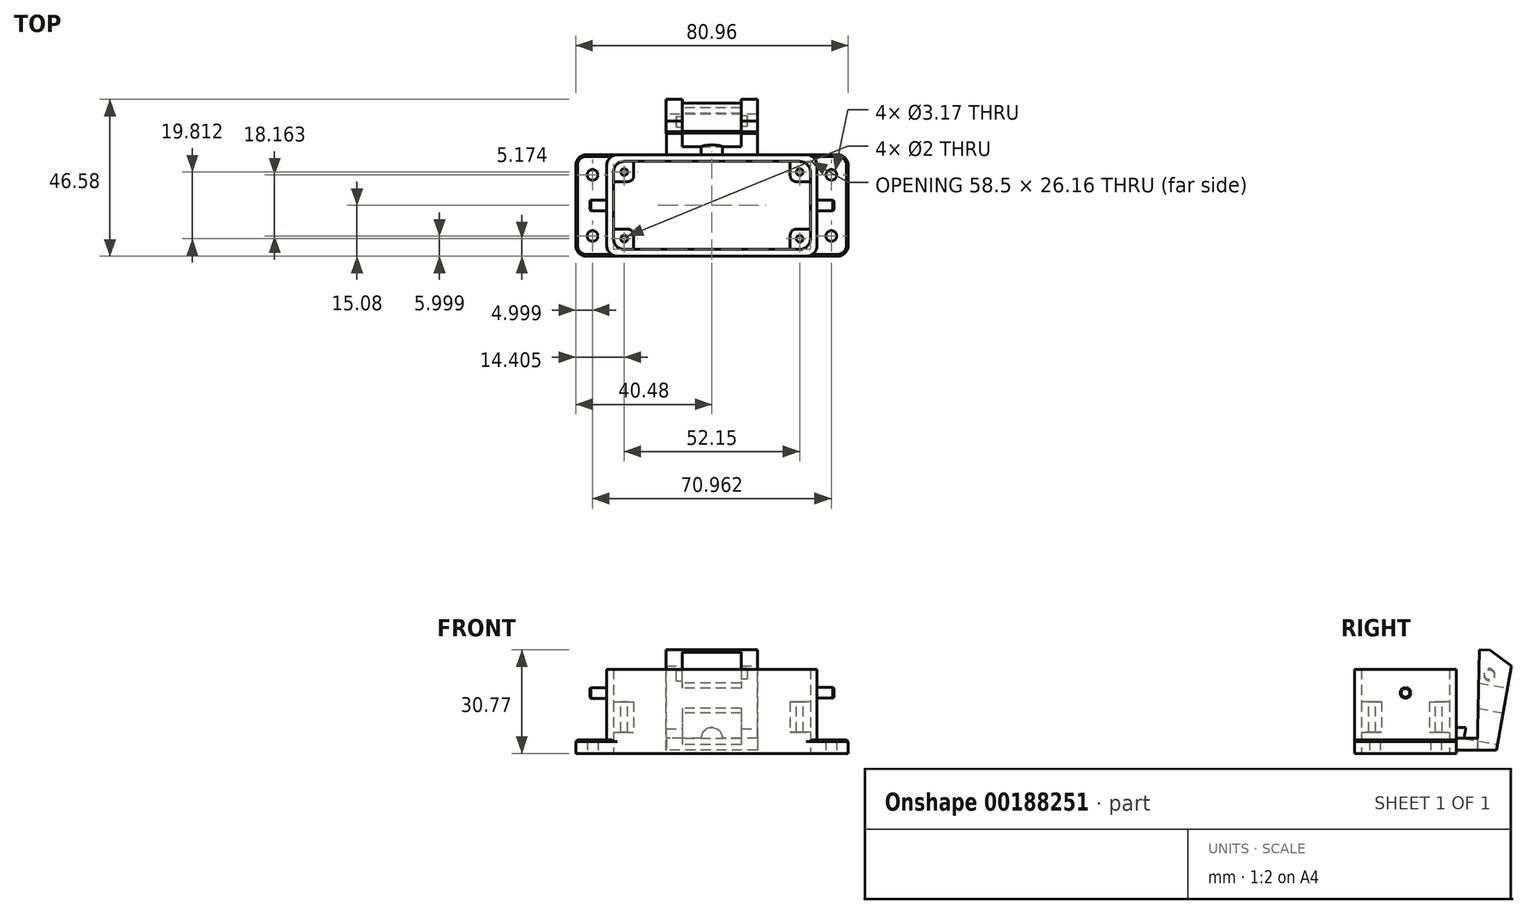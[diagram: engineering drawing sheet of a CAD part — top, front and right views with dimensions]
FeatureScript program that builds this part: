
annotation { "Feature Type Name" : "Feature", "Feature Type Description" : "" }
export const myFeature = defineFeature(function(context is Context, id is Id, definition is map)
    precondition{}
    {
        {
            var Q0;
            Q0=qCreatedBy(makeId("Top.planeOp"),FACE);
            var sketch = newSketch(context, id + "F0", { "sketchPlane" : qUnion([Q0])});
            skLineSegment(sketch, "E0.bottom", {"start": v(-37.3, 15.08) * mm, "end": v(37.3, 15.08) * mm});
            skLineSegment(sketch, "E0.top", {"start": v(-37.3, -15.08) * mm, "end": v(37.3, -15.08) * mm});
            skLineSegment(sketch, "E0.left", {"start": v(-40.48, 11.9) * mm, "end": v(-40.48, -11.9) * mm});
            skLineSegment(sketch, "E0.right", {"start": v(40.48, 11.9) * mm, "end": v(40.48, -11.9) * mm});
            skPoint(sketch, "E0.middle", {"position": v(0, 0) * mm});
            skCircle(sketch, "E1", {"center": v(-35.48, 9.08) * mm, "radius": 1.59 * mm});
            skCircle(sketch, "E2", {"center": v(-35.48, -9.08) * mm, "radius": 1.59 * mm});
            skCircle(sketch, "E3", {"center": v(35.48, -9.08) * mm, "radius": 1.59 * mm});
            skCircle(sketch, "E4", {"center": v(35.48, 9.08) * mm, "radius": 1.59 * mm});
            skPoint(sketch, "E5.visualSharp", {"position": v(-40.48, 15.08) * mm});
            skArc(sketch, "E5.filletArc", {"start": v(-37.3, 15.08) * mm, "mid": v(-39.55, 14.15) * mm, "end": v(-40.48, 11.9) * mm});
            skPoint(sketch, "E6.visualSharp", {"position": v(-40.48, -15.08) * mm});
            skArc(sketch, "E6.filletArc", {"start": v(-40.48, -11.9) * mm, "mid": v(-39.55, -14.15) * mm, "end": v(-37.3, -15.08) * mm});
            skPoint(sketch, "E7.visualSharp", {"position": v(40.48, -15.08) * mm});
            skArc(sketch, "E7.filletArc", {"start": v(37.3, -15.08) * mm, "mid": v(39.55, -14.15) * mm, "end": v(40.48, -11.9) * mm});
            skPoint(sketch, "E8.visualSharp", {"position": v(40.48, 15.08) * mm});
            skArc(sketch, "E8.filletArc", {"start": v(40.48, 11.9) * mm, "mid": v(39.55, 14.15) * mm, "end": v(37.3, 15.08) * mm});
            skLineSegment(sketch, "E9.bottom", {"start": v(-26.07, 13.08) * mm, "end": v(26.07, 13.08) * mm});
            skLineSegment(sketch, "E9.top", {"start": v(-26.07, -13.08) * mm, "end": v(26.07, -13.08) * mm});
            skLineSegment(sketch, "E9.left", {"start": v(-29.25, 9.9) * mm, "end": v(-29.25, -9.9) * mm});
            skLineSegment(sketch, "E9.right", {"start": v(29.25, 9.9) * mm, "end": v(29.25, -9.9) * mm});
            skPoint(sketch, "E10.visualSharp", {"position": v(-29.25, 13.08) * mm});
            skArc(sketch, "E10.filletArc", {"start": v(-26.07, 13.08) * mm, "mid": v(-28.32, 12.15) * mm, "end": v(-29.25, 9.9) * mm});
            skPoint(sketch, "E11.visualSharp", {"position": v(-29.25, -13.08) * mm});
            skArc(sketch, "E11.filletArc", {"start": v(-29.25, -9.9) * mm, "mid": v(-28.32, -12.15) * mm, "end": v(-26.07, -13.08) * mm});
            skPoint(sketch, "E12.visualSharp", {"position": v(29.25, -13.08) * mm});
            skArc(sketch, "E12.filletArc", {"start": v(26.07, -13.08) * mm, "mid": v(28.32, -12.15) * mm, "end": v(29.25, -9.9) * mm});
            skPoint(sketch, "E13.visualSharp", {"position": v(29.25, 13.08) * mm});
            skArc(sketch, "E13.filletArc", {"start": v(29.25, 9.9) * mm, "mid": v(28.32, 12.15) * mm, "end": v(26.07, 13.08) * mm});
            skSolve(sketch);
        }
        {
            var Q0;
            Q0 = qSketchRegion(id + "F0", true);
            extrude(context, id + "F1", {"entities" : qUnion([Q0]), "depth" : 4 * mm});
        }
        {
            var Q0;
            Q0=makeQuery(id+"F1.opExtrude","CAP_FACE",FACE,{"disambiguationData":[OSD([sQuery(id+"F0.wireOp",EDGE,"E0.bottom"),sQuery(id+"F0.wireOp",EDGE,"E0.top"),sQuery(id+"F0.wireOp",EDGE,"E0.left"),sQuery(id+"F0.wireOp",EDGE,"E0.right"),sQuery(id+"F0.wireOp",EDGE,"E1"),sQuery(id+"F0.wireOp",EDGE,"E2"),sQuery(id+"F0.wireOp",EDGE,"E3"),sQuery(id+"F0.wireOp",EDGE,"E4"),sQuery(id+"F0.wireOp",EDGE,"E5.filletArc"),sQuery(id+"F0.wireOp",EDGE,"E6.filletArc"),sQuery(id+"F0.wireOp",EDGE,"E7.filletArc"),sQuery(id+"F0.wireOp",EDGE,"E8.filletArc"),sQuery(id+"F0.wireOp",EDGE,"E9.bottom"),sQuery(id+"F0.wireOp",EDGE,"E9.top"),sQuery(id+"F0.wireOp",EDGE,"E9.left"),sQuery(id+"F0.wireOp",EDGE,"E9.right"),sQuery(id+"F0.wireOp",EDGE,"E10.filletArc"),sQuery(id+"F0.wireOp",EDGE,"E11.filletArc"),sQuery(id+"F0.wireOp",EDGE,"E12.filletArc"),sQuery(id+"F0.wireOp",EDGE,"E13.filletArc")])],"isStart":false});
            var sketch = newSketch(context, id + "F2", { "sketchPlane" : qUnion([Q0])});
            skLineSegment(sketch, "E14.bottom", {"start": v(-26.07, 13.08) * mm, "end": v(26.07, 13.08) * mm});
            skLineSegment(sketch, "E14.top", {"start": v(-26.07, -13.08) * mm, "end": v(26.07, -13.08) * mm});
            skLineSegment(sketch, "E14.left", {"start": v(-29.25, 9.9) * mm, "end": v(-29.25, -9.9) * mm});
            skLineSegment(sketch, "E14.right", {"start": v(29.25, 9.9) * mm, "end": v(29.25, -9.9) * mm});
            skPoint(sketch, "E14.middle", {"position": v(0, 0) * mm});
            skPoint(sketch, "E15.visualSharp", {"position": v(-29.25, 13.08) * mm});
            skArc(sketch, "E15.filletArc", {"start": v(-26.07, 13.08) * mm, "mid": v(-28.32, 12.15) * mm, "end": v(-29.25, 9.9) * mm});
            skPoint(sketch, "E16.visualSharp", {"position": v(-29.25, -13.08) * mm});
            skArc(sketch, "E16.filletArc", {"start": v(-29.25, -9.9) * mm, "mid": v(-28.32, -12.15) * mm, "end": v(-26.07, -13.08) * mm});
            skPoint(sketch, "E17.visualSharp", {"position": v(29.25, -13.08) * mm});
            skArc(sketch, "E17.filletArc", {"start": v(26.07, -13.08) * mm, "mid": v(28.32, -12.15) * mm, "end": v(29.25, -9.9) * mm});
            skPoint(sketch, "E18.visualSharp", {"position": v(29.25, 13.08) * mm});
            skArc(sketch, "E18.filletArc", {"start": v(29.25, 9.9) * mm, "mid": v(28.32, 12.15) * mm, "end": v(26.07, 13.08) * mm});
            skLineSegment(sketch, "E19.bottom", {"start": v(-28.08, 15.08) * mm, "end": v(28.08, 15.08) * mm});
            skLineSegment(sketch, "E19.top", {"start": v(-28.08, -15.08) * mm, "end": v(28.08, -15.08) * mm});
            skLineSegment(sketch, "E19.left", {"start": v(-31.25, 11.9) * mm, "end": v(-31.25, -11.9) * mm});
            skLineSegment(sketch, "E19.right", {"start": v(31.25, 11.9) * mm, "end": v(31.25, -11.9) * mm});
            skPoint(sketch, "E20.visualSharp", {"position": v(-31.25, 15.08) * mm});
            skArc(sketch, "E20.filletArc", {"start": v(-28.08, 15.08) * mm, "mid": v(-30.32, 14.15) * mm, "end": v(-31.25, 11.9) * mm});
            skPoint(sketch, "E21.visualSharp", {"position": v(-31.25, -15.08) * mm});
            skArc(sketch, "E21.filletArc", {"start": v(-31.25, -11.9) * mm, "mid": v(-30.32, -14.15) * mm, "end": v(-28.08, -15.08) * mm});
            skPoint(sketch, "E22.visualSharp", {"position": v(31.25, -15.08) * mm});
            skArc(sketch, "E22.filletArc", {"start": v(28.08, -15.08) * mm, "mid": v(30.32, -14.15) * mm, "end": v(31.25, -11.9) * mm});
            skPoint(sketch, "E23.visualSharp", {"position": v(31.25, 15.08) * mm});
            skArc(sketch, "E23.filletArc", {"start": v(31.25, 11.9) * mm, "mid": v(30.32, 14.15) * mm, "end": v(28.08, 15.08) * mm});
            skSolve(sketch);
        }
        {
            var Q0;
            Q0 = qSketchRegion(id + "F2", true);
            extrude(context, id + "F3", {"entities" : qUnion([Q0]), "operationType" : NewBodyOperationType.ADD, "depth" : 21 * mm});
        }
        {
            var Q0;
            {var subQ0=sQuery(id+"F0.wireOp",EDGE,"E7.filletArc");var subQ1=sQuery(id+"F0.wireOp",EDGE,"E0.top");Q0=makeQuery(id+"F3.boolean.opBoolean","SPLIT",EDGE,{"disambiguationData":[TD([makeQuery(id+"F1.opExtrude","SWEPT_FACE",FACE,{"disambiguationData":[OSD([subQ0])]})])],"derivedFrom":makeQuery(id+"F1.opExtrude","CAP_EDGE",EDGE,{"disambiguationData":[OSD([subQ1])],"isStart":false})});}
            var Q1;
            Q1=makeQuery(id+"F1.opExtrude","CAP_EDGE",EDGE,{"disambiguationData":[OSD([sQuery(id+"F0.wireOp",EDGE,"E7.filletArc")])],"isStart":false});
            var Q2;
            Q2=makeQuery(id+"F1.opExtrude","CAP_EDGE",EDGE,{"disambiguationData":[OSD([sQuery(id+"F0.wireOp",EDGE,"E0.right")])],"isStart":false});
            var Q3;
            Q3=makeQuery(id+"F1.opExtrude","CAP_EDGE",EDGE,{"disambiguationData":[OSD([sQuery(id+"F0.wireOp",EDGE,"E8.filletArc")])],"isStart":false});
            var Q4;
            {var subQ0=sQuery(id+"F0.wireOp",EDGE,"E8.filletArc");var subQ1=sQuery(id+"F0.wireOp",EDGE,"E0.bottom");Q4=makeQuery(id+"F3.boolean.opBoolean","SPLIT",EDGE,{"disambiguationData":[TD([makeQuery(id+"F1.opExtrude","SWEPT_FACE",FACE,{"disambiguationData":[OSD([subQ0])]})])],"derivedFrom":makeQuery(id+"F1.opExtrude","CAP_EDGE",EDGE,{"disambiguationData":[OSD([subQ1])],"isStart":false})});}
            var Q5;
            {var subQ0=sQuery(id+"F0.wireOp",EDGE,"E6.filletArc");var subQ1=sQuery(id+"F0.wireOp",EDGE,"E0.top");Q5=makeQuery(id+"F3.boolean.opBoolean","SPLIT",EDGE,{"disambiguationData":[TD([makeQuery(id+"F1.opExtrude","SWEPT_FACE",FACE,{"disambiguationData":[OSD([subQ0])]})])],"derivedFrom":makeQuery(id+"F1.opExtrude","CAP_EDGE",EDGE,{"disambiguationData":[OSD([subQ1])],"isStart":false})});}
            var Q6;
            Q6=makeQuery(id+"F1.opExtrude","CAP_EDGE",EDGE,{"disambiguationData":[OSD([sQuery(id+"F0.wireOp",EDGE,"E6.filletArc")])],"isStart":false});
            var Q7;
            Q7=makeQuery(id+"F1.opExtrude","CAP_EDGE",EDGE,{"disambiguationData":[OSD([sQuery(id+"F0.wireOp",EDGE,"E0.left")])],"isStart":false});
            var Q8;
            Q8=makeQuery(id+"F1.opExtrude","CAP_EDGE",EDGE,{"disambiguationData":[OSD([sQuery(id+"F0.wireOp",EDGE,"E5.filletArc")])],"isStart":false});
            var Q9;
            {var subQ0=sQuery(id+"F0.wireOp",EDGE,"E5.filletArc");var subQ1=sQuery(id+"F0.wireOp",EDGE,"E0.bottom");Q9=makeQuery(id+"F3.boolean.opBoolean","SPLIT",EDGE,{"disambiguationData":[TD([makeQuery(id+"F1.opExtrude","SWEPT_FACE",FACE,{"disambiguationData":[OSD([subQ0])]})])],"derivedFrom":makeQuery(id+"F1.opExtrude","CAP_EDGE",EDGE,{"disambiguationData":[OSD([subQ1])],"isStart":false})});}
            chamfer(context, id + "F4", {"entities" : qUnion([Q0, Q1, Q2, Q3, Q4, Q5, Q6, Q7, Q8, Q9]), "width" : 0.5 * mm, "tangentPropagation" : true});
        }
        {
            var Q0;
            Q0=makeQuery(id+"F3.opExtrude","SWEPT_FACE",FACE,{"disambiguationData":[OSD([sQuery(id+"F2.wireOp",EDGE,"E19.right")])]});
            var sketch = newSketch(context, id + "F5", { "sketchPlane" : qUnion([Q0])});
            skCircle(sketch, "E24", {"center": v(0, 18) * mm, "radius": 1.59 * mm});
            skSolve(sketch);
        }
        {
            var Q0;
            Q0 = qSketchRegion(id + "F5", true);
            extrude(context, id + "F6", {"entities" : qUnion([Q0]), "operationType" : NewBodyOperationType.ADD, "depth" : 5 * mm});
        }
        {
            var Q0;
            Q0=makeQuery(id+"F3.opExtrude","SWEPT_FACE",FACE,{"disambiguationData":[OSD([sQuery(id+"F2.wireOp",EDGE,"E19.left")])]});
            var sketch = newSketch(context, id + "F7", { "sketchPlane" : qUnion([Q0])});
            skCircle(sketch, "E25", {"center": v(0, 17.99) * mm, "radius": 1.59 * mm});
            skSolve(sketch);
        }
        {
            var Q0;
            Q0 = qSketchRegion(id + "F7", true);
            extrude(context, id + "F8", {"entities" : qUnion([Q0]), "operationType" : NewBodyOperationType.ADD, "depth" : 5 * mm});
        }
        {
            var Q0;
            Q0=makeQuery(id+"F6.opExtrude","CAP_EDGE",EDGE,{"disambiguationData":[OSD([sQuery(id+"F5.wireOp",EDGE,"E24")])],"isStart":false});
            var Q1;
            Q1=makeQuery(id+"F8.opExtrude","CAP_EDGE",EDGE,{"disambiguationData":[OSD([sQuery(id+"F7.wireOp",EDGE,"E25")])],"isStart":false});
            chamfer(context, id + "F9", {"entities" : qUnion([Q0, Q1]), "width" : 0.32 * mm, "tangentPropagation" : true});
        }
        {
            var Q0;
            Q0=qCreatedBy(makeId("Top.planeOp"),FACE);
            cPlane(context, id + "F10", {"entities" : qUnion([Q0]), "cplaneType" : CPlaneType.OFFSET, "offset" : 6.35 * mm, "width" : 152.4 * mm, "height" : 152.4 * mm});
        }
        {
            var Q0;
            Q0=qCreatedBy(id+"F10.planeOp",FACE);
            var sketch = newSketch(context, id + "F11", { "sketchPlane" : qUnion([Q0])});
            skLineSegment(sketch, "E26.bottom", {"start": v(-29.25, 7.08) * mm, "end": v(-24.96, 7.08) * mm});
            skLineSegment(sketch, "E26.top", {"start": v(-29.25, 13.08) * mm, "end": v(-23.25, 13.08) * mm});
            skLineSegment(sketch, "E26.left", {"start": v(-29.25, 7.08) * mm, "end": v(-29.25, 13.08) * mm});
            skLineSegment(sketch, "E26.right", {"start": v(-23.25, 8.8) * mm, "end": v(-23.25, 13.08) * mm});
            skLineSegment(sketch, "E27.bottom", {"start": v(-24.96, -7.08) * mm, "end": v(-29.25, -7.08) * mm});
            skLineSegment(sketch, "E27.top", {"start": v(-23.25, -13.08) * mm, "end": v(-29.25, -13.08) * mm});
            skLineSegment(sketch, "E27.left", {"start": v(-23.25, -8.8) * mm, "end": v(-23.25, -13.08) * mm});
            skLineSegment(sketch, "E27.right", {"start": v(-29.25, -7.08) * mm, "end": v(-29.25, -13.08) * mm});
            skLineSegment(sketch, "E28.bottom", {"start": v(24.96, -7.08) * mm, "end": v(29.25, -7.08) * mm});
            skLineSegment(sketch, "E28.top", {"start": v(23.25, -13.08) * mm, "end": v(29.25, -13.08) * mm});
            skLineSegment(sketch, "E28.left", {"start": v(23.25, -8.8) * mm, "end": v(23.25, -13.08) * mm});
            skLineSegment(sketch, "E28.right", {"start": v(29.25, -7.08) * mm, "end": v(29.25, -13.08) * mm});
            skLineSegment(sketch, "E29.bottom", {"start": v(24.96, 7.08) * mm, "end": v(29.25, 7.08) * mm});
            skLineSegment(sketch, "E29.top", {"start": v(23.25, 13.08) * mm, "end": v(29.25, 13.08) * mm});
            skLineSegment(sketch, "E29.left", {"start": v(23.25, 8.8) * mm, "end": v(23.25, 13.08) * mm});
            skLineSegment(sketch, "E29.right", {"start": v(29.25, 7.08) * mm, "end": v(29.25, 13.08) * mm});
            skPoint(sketch, "E30.visualSharp", {"position": v(-23.25, 7.08) * mm});
            skArc(sketch, "E30.filletArc", {"start": v(-24.96, 7.08) * mm, "mid": v(-23.75, 7.58) * mm, "end": v(-23.25, 8.8) * mm});
            skPoint(sketch, "E31.visualSharp", {"position": v(-23.25, -7.08) * mm});
            skArc(sketch, "E31.filletArc", {"start": v(-23.25, -8.8) * mm, "mid": v(-23.75, -7.58) * mm, "end": v(-24.96, -7.08) * mm});
            skPoint(sketch, "E32.visualSharp", {"position": v(23.25, -7.08) * mm});
            skArc(sketch, "E32.filletArc", {"start": v(24.96, -7.08) * mm, "mid": v(23.75, -7.58) * mm, "end": v(23.25, -8.8) * mm});
            skPoint(sketch, "E33.visualSharp", {"position": v(23.25, 7.08) * mm});
            skArc(sketch, "E33.filletArc", {"start": v(23.25, 8.8) * mm, "mid": v(23.75, 7.58) * mm, "end": v(24.96, 7.08) * mm});
            skSolve(sketch);
        }
        {
            var Q0;
            Q0 = qSketchRegion(id + "F11", true);
            extrude(context, id + "F12", {"entities" : qUnion([Q0]), "operationType" : NewBodyOperationType.ADD, "depth" : 9 * mm});
        }
        {
            var Q0;
            Q0=makeQuery(id+"F12.opExtrude","CAP_FACE",FACE,{"disambiguationData":[OSD([sQuery(id+"F11.wireOp",EDGE,"E26.bottom"),sQuery(id+"F11.wireOp",EDGE,"E26.top"),sQuery(id+"F11.wireOp",EDGE,"E26.left"),sQuery(id+"F11.wireOp",EDGE,"E26.right"),sQuery(id+"F11.wireOp",EDGE,"E30.filletArc")])],"isStart":false});
            var sketch = newSketch(context, id + "F13", { "sketchPlane" : qUnion([Q0])});
            skPoint(sketch, "E34", {"position": v(-26.07, 9.9) * mm});
            skSolve(sketch);
        }
        {
            var Q0;
            Q0=makeQuery(id+"F12.opExtrude","CAP_FACE",FACE,{"disambiguationData":[OSD([sQuery(id+"F11.wireOp",EDGE,"E27.bottom"),sQuery(id+"F11.wireOp",EDGE,"E27.top"),sQuery(id+"F11.wireOp",EDGE,"E27.left"),sQuery(id+"F11.wireOp",EDGE,"E27.right"),sQuery(id+"F11.wireOp",EDGE,"E31.filletArc")])],"isStart":false});
            var sketch = newSketch(context, id + "F14", { "sketchPlane" : qUnion([Q0])});
            skPoint(sketch, "E35", {"position": v(-26.07, -9.9) * mm});
            skSolve(sketch);
        }
        {
            var Q0;
            Q0=makeQuery(id+"F12.opExtrude","CAP_FACE",FACE,{"disambiguationData":[OSD([sQuery(id+"F11.wireOp",EDGE,"E29.bottom"),sQuery(id+"F11.wireOp",EDGE,"E29.top"),sQuery(id+"F11.wireOp",EDGE,"E29.left"),sQuery(id+"F11.wireOp",EDGE,"E29.right"),sQuery(id+"F11.wireOp",EDGE,"E33.filletArc")])],"isStart":false});
            var sketch = newSketch(context, id + "F15", { "sketchPlane" : qUnion([Q0])});
            skPoint(sketch, "E36", {"position": v(26.07, 9.9) * mm});
            skSolve(sketch);
        }
        {
            var Q0;
            Q0=makeQuery(id+"F12.opExtrude","CAP_FACE",FACE,{"disambiguationData":[OSD([sQuery(id+"F11.wireOp",EDGE,"E28.bottom"),sQuery(id+"F11.wireOp",EDGE,"E28.top"),sQuery(id+"F11.wireOp",EDGE,"E28.left"),sQuery(id+"F11.wireOp",EDGE,"E28.right"),sQuery(id+"F11.wireOp",EDGE,"E32.filletArc")])],"isStart":false});
            var sketch = newSketch(context, id + "F16", { "sketchPlane" : qUnion([Q0])});
            skPoint(sketch, "E37", {"position": v(26.07, -9.9) * mm});
            skSolve(sketch);
        }
        {
            var Q0;
            Q0=sQuery(id+"F13.wireOp",VERTEX,"E34");
            var Q1;
            Q1=sQuery(id+"F14.wireOp",VERTEX,"E35");
            var Q2;
            Q2=sQuery(id+"F16.wireOp",VERTEX,"E37");
            var Q3;
            Q3=sQuery(id+"F15.wireOp",VERTEX,"E36");
            var Q4;
            Q4=makeQuery(id+"F1.opExtrude","SWEPT_BODY",BODY,{"disambiguationData":[OSD([sQuery(id+"F0.wireOp",EDGE,"E0.bottom"),sQuery(id+"F0.wireOp",EDGE,"E0.top"),sQuery(id+"F0.wireOp",EDGE,"E0.left"),sQuery(id+"F0.wireOp",EDGE,"E0.right"),sQuery(id+"F0.wireOp",EDGE,"E1"),sQuery(id+"F0.wireOp",EDGE,"E2"),sQuery(id+"F0.wireOp",EDGE,"E3"),sQuery(id+"F0.wireOp",EDGE,"E4"),sQuery(id+"F0.wireOp",EDGE,"E5.filletArc"),sQuery(id+"F0.wireOp",EDGE,"E6.filletArc"),sQuery(id+"F0.wireOp",EDGE,"E7.filletArc"),sQuery(id+"F0.wireOp",EDGE,"E8.filletArc"),sQuery(id+"F0.wireOp",EDGE,"E9.bottom"),sQuery(id+"F0.wireOp",EDGE,"E9.top"),sQuery(id+"F0.wireOp",EDGE,"E9.left"),sQuery(id+"F0.wireOp",EDGE,"E9.right"),sQuery(id+"F0.wireOp",EDGE,"E10.filletArc"),sQuery(id+"F0.wireOp",EDGE,"E11.filletArc"),sQuery(id+"F0.wireOp",EDGE,"E12.filletArc"),sQuery(id+"F0.wireOp",EDGE,"E13.filletArc")])]});
            hole(context, id + "F17", {"style" : HoleStyle.SIMPLE, "endStyle" : HoleEndStyle.THROUGH, "holeDiameter" : 2 * mm, "locations" : qUnion([Q0, Q1, Q2, Q3]), "scope" : qUnion([Q4]), "isTappedThrough" : true});
        }
        {
            var Q0;
            Q0=makeQuery(id+"F3.boolean.opBoolean","MERGE",FACE,{"derivedFrom":[makeQuery(id+"F1.opExtrude","SWEPT_FACE",FACE,{"disambiguationData":[OSD([sQuery(id+"F0.wireOp",EDGE,"E0.bottom")])]}),makeQuery(id+"F3.opExtrude","SWEPT_FACE",FACE,{"disambiguationData":[OSD([sQuery(id+"F2.wireOp",EDGE,"E19.bottom")])]})]});
            var sketch = newSketch(context, id + "F18", { "sketchPlane" : qUnion([Q0])});
            skLineSegment(sketch, "E38.bottom", {"start": v(-13.5, 4.5) * mm, "end": v(-3.17, 4.5) * mm});
            skLineSegment(sketch, "E38.top", {"start": v(-13.5, 1) * mm, "end": v(13.5, 1) * mm});
            skLineSegment(sketch, "E38.left", {"start": v(-13.5, 4.5) * mm, "end": v(-13.5, 1) * mm});
            skLineSegment(sketch, "E38.right", {"start": v(13.5, 4.5) * mm, "end": v(13.5, 1) * mm});
            skArc(sketch, "E39", {"start": v(3.18, 4.5) * mm, "mid": v(0, 7.67) * mm, "end": v(-3.17, 4.5) * mm});
            skLineSegment(sketch, "E40.trimOffspring", {"start": v(3.18, 4.5) * mm, "end": v(13.5, 4.5) * mm});
            skSolve(sketch);
        }
        {
            var Q0;
            Q0 = qSketchRegion(id + "F18", true);
            extrude(context, id + "F19", {"entities" : qUnion([Q0]), "operationType" : NewBodyOperationType.ADD, "depth" : 12 * mm});
        }
        {
            var Q0;
            Q0=makeQuery(id+"F19.opExtrude","SWEPT_FACE",FACE,{"disambiguationData":[OSD([sQuery(id+"F18.wireOp",EDGE,"E38.left")])]});
            var sketch = newSketch(context, id + "F20", { "sketchPlane" : qUnion([Q0])});
            skLineSegment(sketch, "E41", {"start": v(21.43, 1) * mm, "end": v(21.43, 7.35) * mm});
            skLineSegment(sketch, "E42", {"start": v(21.43, 7.35) * mm, "end": v(21.92, 30.77) * mm});
            skLineSegment(sketch, "E43", {"start": v(21.92, 30.77) * mm, "end": v(25.1, 30.7) * mm});
            skLineSegment(sketch, "E44", {"start": v(25.1, 30.7) * mm, "end": v(31.5, 26.01) * mm});
            skLineSegment(sketch, "E45", {"start": v(31.5, 26.01) * mm, "end": v(27.09, 1) * mm});
            skLineSegment(sketch, "E46", {"start": v(27.09, 1) * mm, "end": v(21.43, 1) * mm});
            skSolve(sketch);
        }
        {
            var Q0;
            Q0 = qSketchRegion(id + "F20", true);
            extrude(context, id + "F21", {"entities" : qUnion([Q0]), "operationType" : NewBodyOperationType.ADD, "oppositeDirection" : true, "depth" : 27.1 * mm});
        }
        {
            var Q0;
            Q0=makeQuery(id+"F21.opExtrude","SWEPT_FACE",FACE,{"disambiguationData":[OSD([sQuery(id+"F20.wireOp",EDGE,"E45")])]});
            var sketch = newSketch(context, id + "F22", { "sketchPlane" : qUnion([Q0])});
            skLineSegment(sketch, "E47.bottom", {"start": v(-8.73, 16.93) * mm, "end": v(8.86, 16.93) * mm});
            skLineSegment(sketch, "E47.top", {"start": v(-8.73, 7.4) * mm, "end": v(8.86, 7.4) * mm});
            skLineSegment(sketch, "E47.left", {"start": v(-8.73, 16.93) * mm, "end": v(-8.73, 7.4) * mm});
            skLineSegment(sketch, "E47.right", {"start": v(8.86, 16.93) * mm, "end": v(8.86, 7.4) * mm});
            skLineSegment(sketch, "E48", {"start": v(-8.73, 37.12) * mm, "end": v(-8.73, 24.42) * mm});
            skLineSegment(sketch, "E49", {"start": v(-8.73, 24.42) * mm, "end": v(8.86, 24.42) * mm});
            skLineSegment(sketch, "E50", {"start": v(8.86, 24.42) * mm, "end": v(8.86, 37.12) * mm});
            skLineSegment(sketch, "E51", {"start": v(8.86, 37.12) * mm, "end": v(-8.73, 37.12) * mm});
            skSolve(sketch);
        }
        {
            var Q0;
            Q0 = qSketchRegion(id + "F22", true);
            extrude(context, id + "F23", {"entities" : qUnion([Q0]), "operationType" : NewBodyOperationType.REMOVE, "oppositeDirection" : true, "depth" : 10.16 * mm});
        }
        {
            var Q0;
            Q0=makeQuery(id+"F23.boolean.opBoolean","COPY",FACE,{"derivedFrom":makeQuery(id+"F23.opExtrude","SWEPT_FACE",FACE,{"disambiguationData":[OSD([sQuery(id+"F22.wireOp",EDGE,"E50")])]})});
            var sketch = newSketch(context, id + "F24", { "sketchPlane" : qUnion([Q0])});
            skCircle(sketch, "E52", {"center": v(24.94, 23.2) * mm, "radius": 1.59 * mm});
            skSolve(sketch);
        }
        {
            var Q0;
            Q0=makeQuery(id+"F23.boolean.opBoolean","COPY",FACE,{"derivedFrom":makeQuery(id+"F23.opExtrude","SWEPT_FACE",FACE,{"disambiguationData":[OSD([sQuery(id+"F22.wireOp",EDGE,"E48")])]})});
            var sketch = newSketch(context, id + "F25", { "sketchPlane" : qUnion([Q0])});
            skCircle(sketch, "E53", {"center": v(-24.95, 23.62) * mm, "radius": 1.59 * mm});
            skSolve(sketch);
        }
        {
            var Q0;
            Q0=makeQuery(id+"F25.imprint","IMPRINT",FACE,{"disambiguationData":[TD([[makeQuery(id+"F25.imprint","IMPRINT",EDGE,{"derivedFrom":sQuery(id+"F25.wireOp",EDGE,"E53")}),1.0]])]});
            extrude(context, id + "F26", {"entities" : qUnion([Q0]), "operationType" : NewBodyOperationType.REMOVE, "oppositeDirection" : true, "depth" : 1.71 * mm});
        }
        {
            var Q0;
            Q0=makeQuery(id+"F24.imprint","IMPRINT",FACE,{"disambiguationData":[TD([[makeQuery(id+"F24.imprint","IMPRINT",EDGE,{"derivedFrom":sQuery(id+"F24.wireOp",EDGE,"E52")}),1.0]])]});
            extrude(context, id + "F27", {"entities" : qUnion([Q0]), "operationType" : NewBodyOperationType.REMOVE, "oppositeDirection" : true, "depth" : 1.71 * mm});
        }
    });
